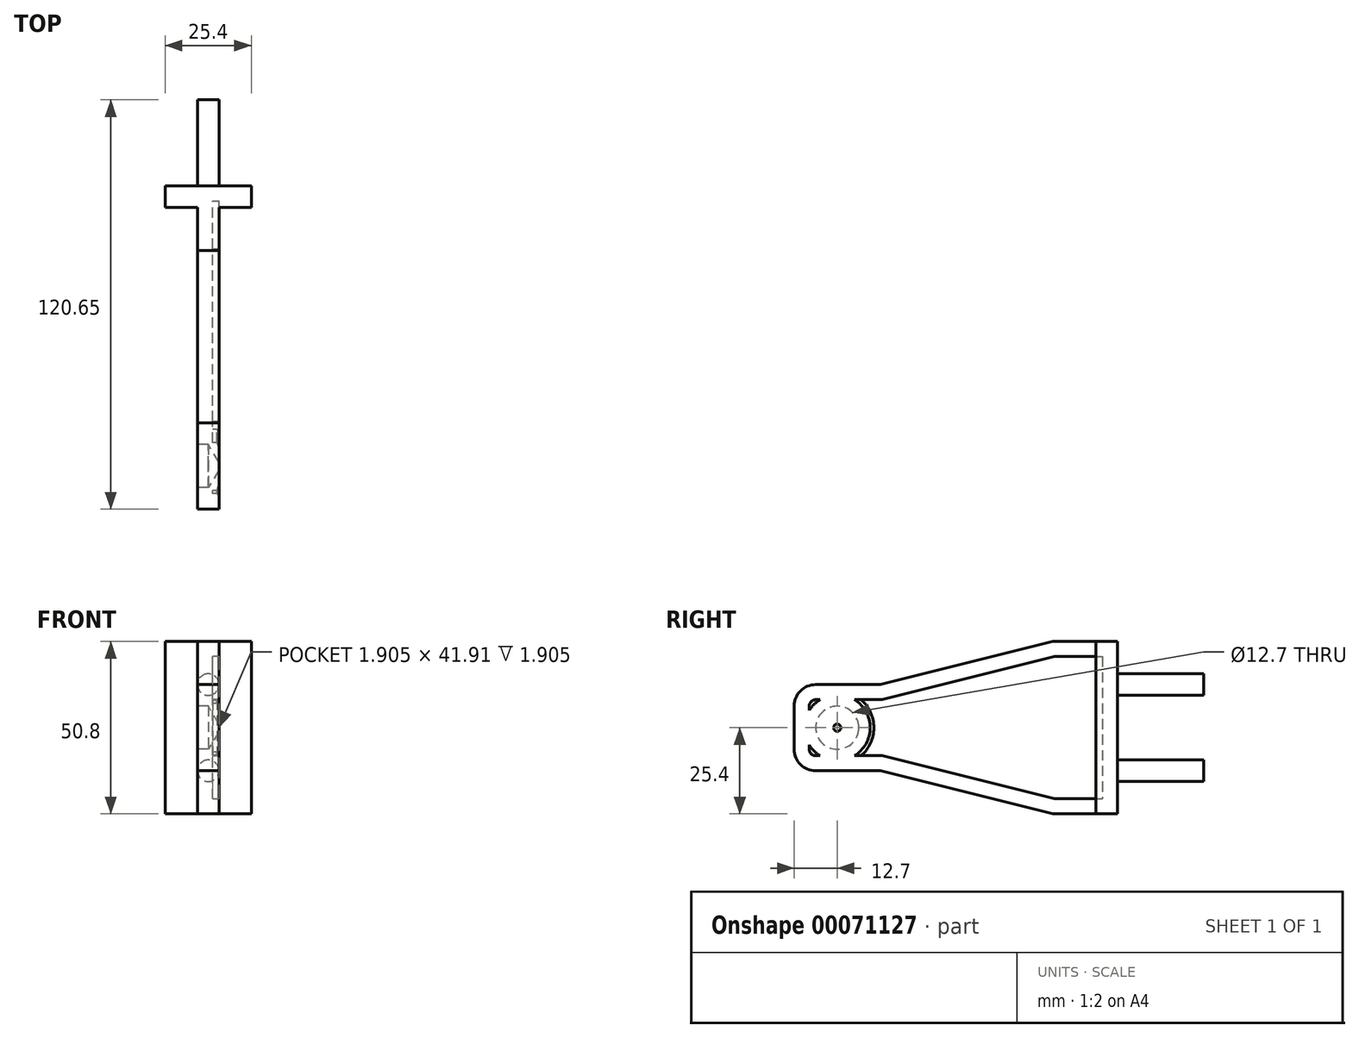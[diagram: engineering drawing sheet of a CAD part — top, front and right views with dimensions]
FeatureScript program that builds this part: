
annotation { "Feature Type Name" : "Feature", "Feature Type Description" : "" }
export const myFeature = defineFeature(function(context is Context, id is Id, definition is map)
    precondition{}
    {
        {
            var Q0;
            Q0=qCreatedBy(makeId("Front.planeOp"),FACE);
            var sketch = newSketch(context, id + "F0", { "sketchPlane" : qUnion([Q0])});
            skLineSegment(sketch, "E0.bottom", {"start": v(0, 0) * mm, "end": v(25.4, 0) * mm});
            skLineSegment(sketch, "E0.top", {"start": v(0, 50.8) * mm, "end": v(25.4, 50.8) * mm});
            skLineSegment(sketch, "E0.left", {"start": v(0, 0) * mm, "end": v(0, 50.8) * mm});
            skLineSegment(sketch, "E0.right", {"start": v(25.4, 0) * mm, "end": v(25.4, 50.8) * mm});
            skSolve(sketch);
        }
        {
            var Q0;
            Q0 = qSketchRegion(id + "F0", true);
            extrude(context, id + "F1", {"entities" : qUnion([Q0]), "depth" : 6.35 * mm});
        }
        {
            var Q0;
            Q0=makeQuery(id+"F1.opExtrude","CAP_FACE",FACE,{"disambiguationData":[OSD([sQuery(id+"F0.wireOp",EDGE,"E0.bottom"),sQuery(id+"F0.wireOp",EDGE,"E0.top"),sQuery(id+"F0.wireOp",EDGE,"E0.left"),sQuery(id+"F0.wireOp",EDGE,"E0.right")])],"isStart":false});
            var sketch = newSketch(context, id + "F2", { "sketchPlane" : qUnion([Q0])});
            skLineSegment(sketch, "E1.bottom", {"start": v(9.53, 0) * mm, "end": v(15.88, 0) * mm});
            skLineSegment(sketch, "E1.top", {"start": v(9.53, 50.8) * mm, "end": v(15.88, 50.8) * mm});
            skLineSegment(sketch, "E1.left", {"start": v(9.53, 0) * mm, "end": v(9.52, 50.8) * mm});
            skLineSegment(sketch, "E1.right", {"start": v(15.88, 0) * mm, "end": v(15.88, 50.8) * mm});
            skSolve(sketch);
        }
        {
            var Q0;
            Q0 = qSketchRegion(id + "F2", true);
            extrude(context, id + "F3", {"entities" : qUnion([Q0]), "operationType" : NewBodyOperationType.ADD, "depth" : 12.7 * mm});
        }
        {
            var Q0;
            Q0=makeQuery(id+"F3.opExtrude","CAP_FACE",FACE,{"disambiguationData":[OSD([sQuery(id+"F2.wireOp",EDGE,"E1.bottom"),sQuery(id+"F2.wireOp",EDGE,"E1.top"),sQuery(id+"F2.wireOp",EDGE,"E1.left"),sQuery(id+"F2.wireOp",EDGE,"E1.right")])],"isStart":false});
            cPlane(context, id + "F4", {"entities" : qUnion([Q0]), "cplaneType" : CPlaneType.OFFSET, "offset" : 50.8 * mm, "width" : 152.4 * mm, "height" : 152.4 * mm});
        }
        {
            var Q0;
            Q0=qCreatedBy(id+"F4.planeOp",FACE);
            var sketch = newSketch(context, id + "F5", { "sketchPlane" : qUnion([Q0])});
            skLineSegment(sketch, "E2.0", {"start": v(9.53, 12.7) * mm, "end": v(9.53, 38.1) * mm});
            skLineSegment(sketch, "E3.0", {"start": v(15.88, 12.7) * mm, "end": v(15.88, 38.1) * mm});
            skLineSegment(sketch, "E4", {"start": v(9.53, 38.1) * mm, "end": v(15.88, 38.1) * mm});
            skLineSegment(sketch, "E5", {"start": v(9.53, 12.7) * mm, "end": v(15.88, 12.7) * mm});
            skSolve(sketch);
        }
        {
            var Q1;
            Q1=makeQuery(id+"F3.opExtrude","CAP_FACE",FACE,{"disambiguationData":[OSD([sQuery(id+"F2.wireOp",EDGE,"E1.bottom"),sQuery(id+"F2.wireOp",EDGE,"E1.top"),sQuery(id+"F2.wireOp",EDGE,"E1.left"),sQuery(id+"F2.wireOp",EDGE,"E1.right")])],"isStart":false});
            var Q2;
            Q2=makeQuery(id+"F5.imprint","IMPRINT",FACE,{"disambiguationData":[TD([[makeQuery(id+"F5.imprint","IMPRINT",EDGE,{"derivedFrom":sQuery(id+"F5.wireOp",EDGE,"E2.0")}),-1.0]])]});
            loft(context, id + "F6", {"operationType" : NewBodyOperationType.ADD, "sheetProfilesArray" : [{ "sheetProfileEntities" : qUnion([Q1]) }, { "sheetProfileEntities" : qUnion([Q2]) }]});
        }
        {
            var Q0;
            Q0=makeQuery(id+"F6.opLoft","CAP_FACE",FACE,{"disambiguationData":[OSD([makeQuery(id+"F5.imprint","IMPRINT",FACE,{"disambiguationData":[TD([[makeQuery(id+"F5.imprint","IMPRINT",EDGE,{"derivedFrom":sQuery(id+"F5.wireOp",EDGE,"E2.0")}),-1.0]])]})])],"isStart":true});
            extrude(context, id + "F7", {"entities" : qUnion([Q0]), "operationType" : NewBodyOperationType.ADD, "depth" : 25.4 * mm});
        }
        {
            var Q0;
            Q0=makeQuery(id+"F7.opExtrude","CAP_EDGE",EDGE,{"disambiguationData":[OSD([sQuery(id+"F5.wireOp",EDGE,"E2.0"),sQuery(id+"F5.wireOp",EDGE,"E3.0"),sQuery(id+"F5.wireOp",EDGE,"E5")])],"isStart":false});
            var Q1;
            Q1=makeQuery(id+"F7.opExtrude","CAP_EDGE",EDGE,{"disambiguationData":[OSD([sQuery(id+"F5.wireOp",EDGE,"E2.0"),sQuery(id+"F5.wireOp",EDGE,"E3.0"),sQuery(id+"F5.wireOp",EDGE,"E4")])],"isStart":false});
            fillet(context, id + "F8", {"entities" : qUnion([Q0, Q1]), "radius" : 6.35 * mm, "tangentPropagation" : true, "allowEdgeOverflow" : false});
        }
        {
            var Q0;
            {var subQ0=sQuery(id+"F5.wireOp",EDGE,"E5");var subQ1=sQuery(id+"F5.wireOp",EDGE,"E4");var subQ2=sQuery(id+"F5.wireOp",EDGE,"E2.0");var subQ3=sQuery(id+"F2.wireOp",EDGE,"E1.left");Q0=makeQuery(id+"F7.boolean.opBoolean","MERGE",FACE,{"derivedFrom":[makeQuery(id+"F6.boolean.opBoolean","MERGE",FACE,{"derivedFrom":[makeQuery(id+"F3.opExtrude","SWEPT_FACE",FACE,{"disambiguationData":[OSD([subQ3])]}),makeQuery(id+"F6.opLoft","SWEPT_FACE",FACE,{"disambiguationData":[OSD([sQuery(id+"F0.wireOp",EDGE,"E0.bottom"),sQuery(id+"F0.wireOp",EDGE,"E0.top"),sQuery(id+"F2.wireOp",EDGE,"E1.bottom"),sQuery(id+"F2.wireOp",EDGE,"E1.top"),subQ3,subQ2,subQ1,subQ0])]})]}),makeQuery(id+"F7.opExtrude","SWEPT_FACE",FACE,{"disambiguationData":[OSD([subQ2,subQ1,subQ0])]})]});}
            var sketch = newSketch(context, id + "F9", { "sketchPlane" : qUnion([Q0])});
            skPoint(sketch, "E6", {"position": v(95.25, 25.4) * mm});
            skPoint(sketch, "E7", {"position": v(82.55, 25.4) * mm});
            skSolve(sketch);
        }
        {
            var Q0;
            Q0=sQuery(id+"F9.wireOp",VERTEX,"E7");
            var Q1;
            Q1=makeQuery(id+"F1.opExtrude","SWEPT_BODY",BODY,{"disambiguationData":[OSD([sQuery(id+"F0.wireOp",EDGE,"E0.bottom"),sQuery(id+"F0.wireOp",EDGE,"E0.top"),sQuery(id+"F0.wireOp",EDGE,"E0.left"),sQuery(id+"F0.wireOp",EDGE,"E0.right")])]});
            hole(context, id + "F10", {"style" : HoleStyle.SIMPLE, "holeDiameter" : 12.7 * mm, "endStyle" : HoleEndStyle.BLIND, "holeDepth" : 3.17 * mm, "locations" : qUnion([Q0]), "scope" : qUnion([Q1])});
        }
        {
            var Q0;
            Q0=makeQuery(id+"F1.opExtrude","CAP_FACE",FACE,{"disambiguationData":[OSD([sQuery(id+"F0.wireOp",EDGE,"E0.bottom"),sQuery(id+"F0.wireOp",EDGE,"E0.top"),sQuery(id+"F0.wireOp",EDGE,"E0.left"),sQuery(id+"F0.wireOp",EDGE,"E0.right")])],"isStart":true});
            var sketch = newSketch(context, id + "F11", { "sketchPlane" : qUnion([Q0])});
            skCircle(sketch, "E8", {"center": v(-12.7, 12.7) * mm, "radius": 3.18 * mm});
            skPoint(sketch, "E8.centerSnap0", {"position": v(-12.7, 0) * mm});
            skCircle(sketch, "E9", {"center": v(-12.7, 38.1) * mm, "radius": 3.18 * mm});
            skPoint(sketch, "E9.centerSnap0", {"position": v(-12.7, 50.8) * mm});
            skSolve(sketch);
        }
        {
            var Q0;
            Q0 = qSketchRegion(id + "F11", true);
            extrude(context, id + "F12", {"entities" : qUnion([Q0]), "operationType" : NewBodyOperationType.ADD, "depth" : 25.4 * mm});
        }
        {
            var Q0;
            {var subQ0=sQuery(id+"F5.wireOp",EDGE,"E5");var subQ1=sQuery(id+"F5.wireOp",EDGE,"E4");var subQ2=sQuery(id+"F5.wireOp",EDGE,"E3.0");var subQ3=sQuery(id+"F2.wireOp",EDGE,"E1.right");Q0=makeQuery(id+"F7.boolean.opBoolean","MERGE",FACE,{"derivedFrom":[makeQuery(id+"F6.boolean.opBoolean","MERGE",FACE,{"derivedFrom":[makeQuery(id+"F3.opExtrude","SWEPT_FACE",FACE,{"disambiguationData":[OSD([subQ3])]}),makeQuery(id+"F6.opLoft","SWEPT_FACE",FACE,{"disambiguationData":[OSD([sQuery(id+"F0.wireOp",EDGE,"E0.bottom"),sQuery(id+"F0.wireOp",EDGE,"E0.top"),sQuery(id+"F2.wireOp",EDGE,"E1.bottom"),sQuery(id+"F2.wireOp",EDGE,"E1.top"),subQ3,subQ2,subQ1,subQ0])]})]}),makeQuery(id+"F7.opExtrude","SWEPT_FACE",FACE,{"disambiguationData":[OSD([subQ2,subQ1,subQ0])]})]});}
            shell(context, id + "F13", {"entities" : qUnion([Q0]), "thickness" : 4.44 * mm});
        }
    });
